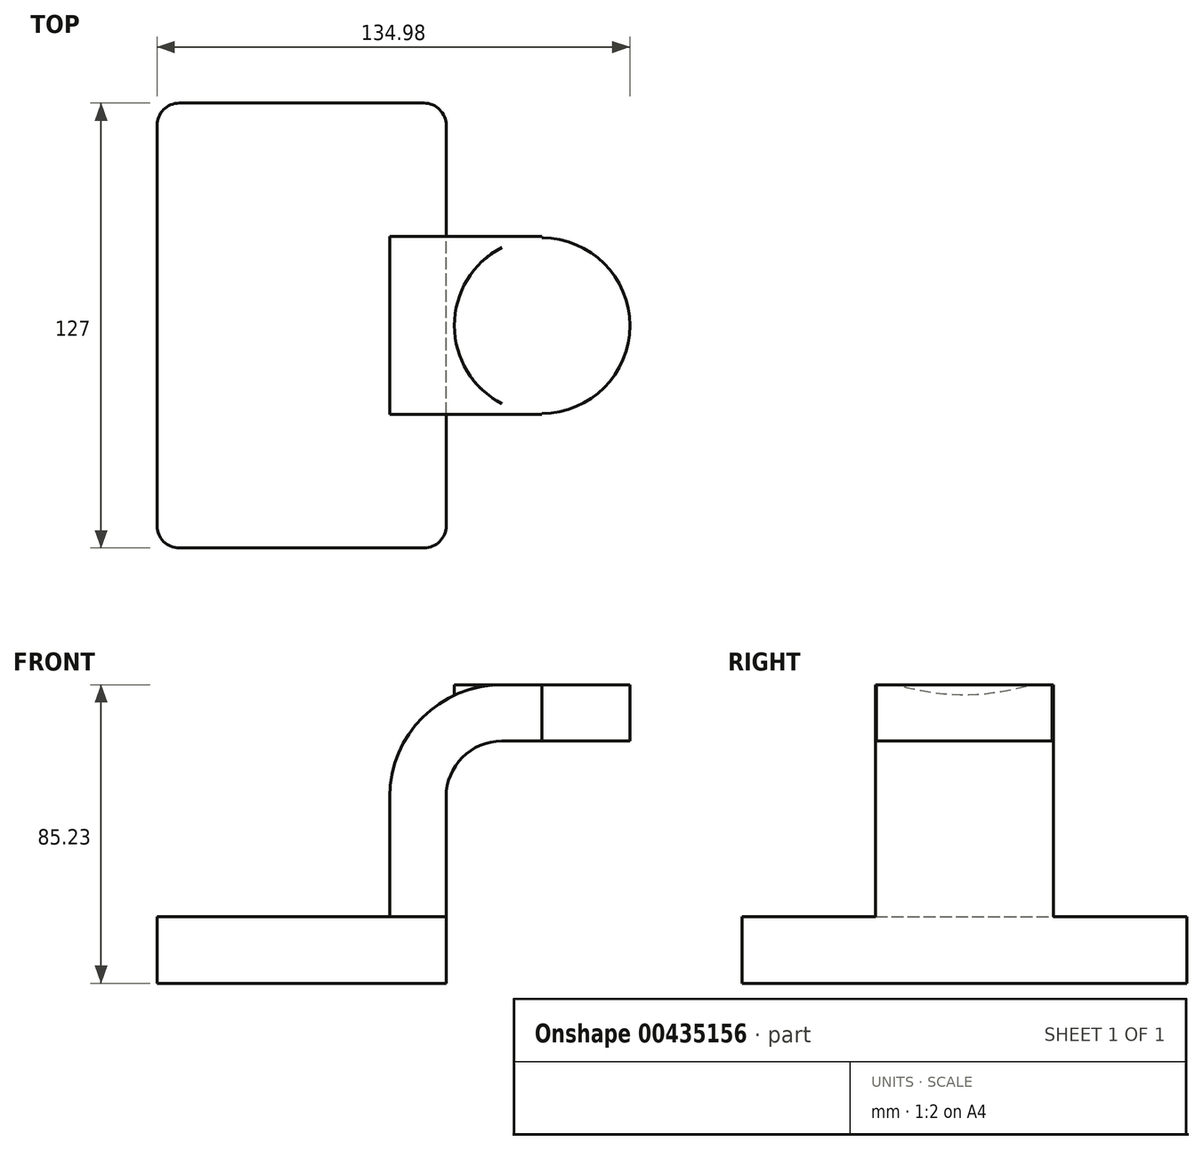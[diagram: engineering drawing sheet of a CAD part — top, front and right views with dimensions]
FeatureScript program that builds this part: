
annotation { "Feature Type Name" : "Feature", "Feature Type Description" : "" }
export const myFeature = defineFeature(function(context is Context, id is Id, definition is map)
    precondition{}
    {
        {
            var Q0;
            Q0=qCreatedBy(makeId("Front.planeOp"),FACE);
            var sketch = newSketch(context, id + "F0", { "sketchPlane" : qUnion([Q0])});
            skLineSegment(sketch, "E0.bottom", {"start": v(-41.28, 9.52) * mm, "end": v(41.28, 9.53) * mm});
            skLineSegment(sketch, "E0.top", {"start": v(-41.28, -9.53) * mm, "end": v(41.28, -9.52) * mm});
            skLineSegment(sketch, "E0.left", {"start": v(-41.28, 9.52) * mm, "end": v(-41.28, -9.53) * mm});
            skLineSegment(sketch, "E0.right", {"start": v(41.28, 9.53) * mm, "end": v(41.28, -9.52) * mm});
            skPoint(sketch, "E0.middle", {"position": v(0, 0) * mm});
            skLineSegment(sketch, "E1.bottom", {"start": v(68.65, 53.48) * mm, "end": v(119.45, 53.48) * mm});
            skLineSegment(sketch, "E1.top", {"start": v(68.65, 82.06) * mm, "end": v(119.45, 82.06) * mm});
            skLineSegment(sketch, "E1.left", {"start": v(68.65, 53.48) * mm, "end": v(68.65, 82.06) * mm});
            skLineSegment(sketch, "E1.right", {"start": v(119.45, 53.48) * mm, "end": v(119.45, 82.06) * mm});
            skPoint(sketch, "E1.middle", {"position": v(94.05, 67.77) * mm});
            skLineSegment(sketch, "E2", {"start": v(41.28, 9.53) * mm, "end": v(41.28, 43.7) * mm});
            skArc(sketch, "E3", {"start": v(41.27, 43.7) * mm, "mid": v(45.92, 54.93) * mm, "end": v(57.15, 59.58) * mm});
            skLineSegment(sketch, "E4", {"start": v(57.15, 59.58) * mm, "end": v(93.71, 59.58) * mm});
            skLineSegment(sketch, "E5.0", {"start": v(57.15, 75.7) * mm, "end": v(93.71, 75.7) * mm});
            skArc(sketch, "E5.1", {"start": v(25.16, 43.7) * mm, "mid": v(34.53, 66.33) * mm, "end": v(57.15, 75.7) * mm});
            skLineSegment(sketch, "E5.2", {"start": v(25.16, 9.53) * mm, "end": v(25.16, 43.7) * mm});
            skLineSegment(sketch, "E6", {"start": v(93.71, 82.06) * mm, "end": v(93.71, 53.48) * mm});
            skPoint(sketch, "E6.startSnap0", {"position": v(94.05, 82.06) * mm});
            skFitSpline(sketch, "E7", {"points": [v(-41.28, 9.52) * mm, v(57.15, 75.7) * mm], "startDerivative": vector(98.42, 66.17) * mm, "endDerivative": vector(319.37, -1.33) * mm});
            skSolve(sketch);
        }
        {
            var Q0;
            Q0=makeQuery(id+"F0.imprint","IMPRINT",FACE,{"disambiguationData":[TD([[makeQuery(id+"F0.imprint","IMPRINT",EDGE,{"derivedFrom":sQuery(id+"F0.wireOp",EDGE,"E0.top")}),1.0]])]});
            extrude(context, id + "F1", {"entities" : qUnion([Q0]), "endBound" : BoundingType.SYMMETRIC, "depth" : 127 * mm});
        }
        {
            var Q0;
            {var subQ1=sQuery(id+"F0.wireOp",EDGE,"E2");Q0=makeQuery(id+"F0.imprint","IMPRINT",FACE,{"disambiguationData":[TD([[makeQuery(id+"F0.imprint","IMPRINT",EDGE,{"derivedFrom":subQ1}),1.0]])]});}
            extrude(context, id + "F2", {"entities" : qUnion([Q0]), "operationType" : NewBodyOperationType.ADD, "endBound" : BoundingType.SYMMETRIC, "depth" : 50.8 * mm});
        }
        {
            var Q0;
            Q0=makeQuery(id+"F0.imprint","IMPRINT",FACE,{"disambiguationData":[TD([[makeQuery(id+"F0.imprint","IMPRINT",EDGE,{"derivedFrom":sQuery(id+"F0.wireOp",EDGE,"E5.1")}),1.0]])]});
            extrude(context, id + "F3", {"entities" : qUnion([Q0]), "operationType" : NewBodyOperationType.ADD, "endBound" : BoundingType.SYMMETRIC, "depth" : 15.88 * mm});
        }
        {
            var Q0;
            {var subQ0=sQuery(id+"F0.wireOp",EDGE,"E4");var subQ1=sQuery(id+"F0.wireOp",EDGE,"E1.left");var subQ2=makeQuery(id+"F0.imprint","INTERSECT",VERTEX,{"derivedFrom":[subQ1,subQ0]});Q0=makeQuery(id+"F0.imprint","IMPRINT",FACE,{"disambiguationData":[TD([[makeQuery(id+"F0.imprint","IMPRINT",EDGE,{"disambiguationData":[TD([[subQ2,-1.0]])],"derivedFrom":subQ1}),-1.0]])]});}
            var Q1;
            Q1=sQuery(id+"F0.wireOp",EDGE,"E1.left");
            revolve(context, id + "F4", {"operationType" : NewBodyOperationType.ADD, "entities" : qUnion([Q0]), "axis" : qUnion([Q1]), "revolveType" : RevolveType.FULL});
        }
        {
            var Q0;
            Q0=makeQuery(id+"F1.opExtrude","CAP_EDGE",EDGE,{"disambiguationData":[OSD([sQuery(id+"F0.wireOp",EDGE,"E0.right")])],"isStart":false});
            var Q1;
            Q1=makeQuery(id+"F1.opExtrude","CAP_EDGE",EDGE,{"disambiguationData":[OSD([sQuery(id+"F0.wireOp",EDGE,"E0.left")])],"isStart":false});
            var Q2;
            Q2=makeQuery(id+"F1.opExtrude","CAP_EDGE",EDGE,{"disambiguationData":[OSD([sQuery(id+"F0.wireOp",EDGE,"E0.right")])],"isStart":true});
            var Q3;
            Q3=makeQuery(id+"F1.opExtrude","CAP_EDGE",EDGE,{"disambiguationData":[OSD([sQuery(id+"F0.wireOp",EDGE,"E0.left")])],"isStart":true});
            fillet(context, id + "F5", {"entities" : qUnion([Q0, Q1, Q2, Q3]), "radius" : 6.35 * mm, "tangentPropagation" : true, "allowEdgeOverflow" : false});
        }
    });
